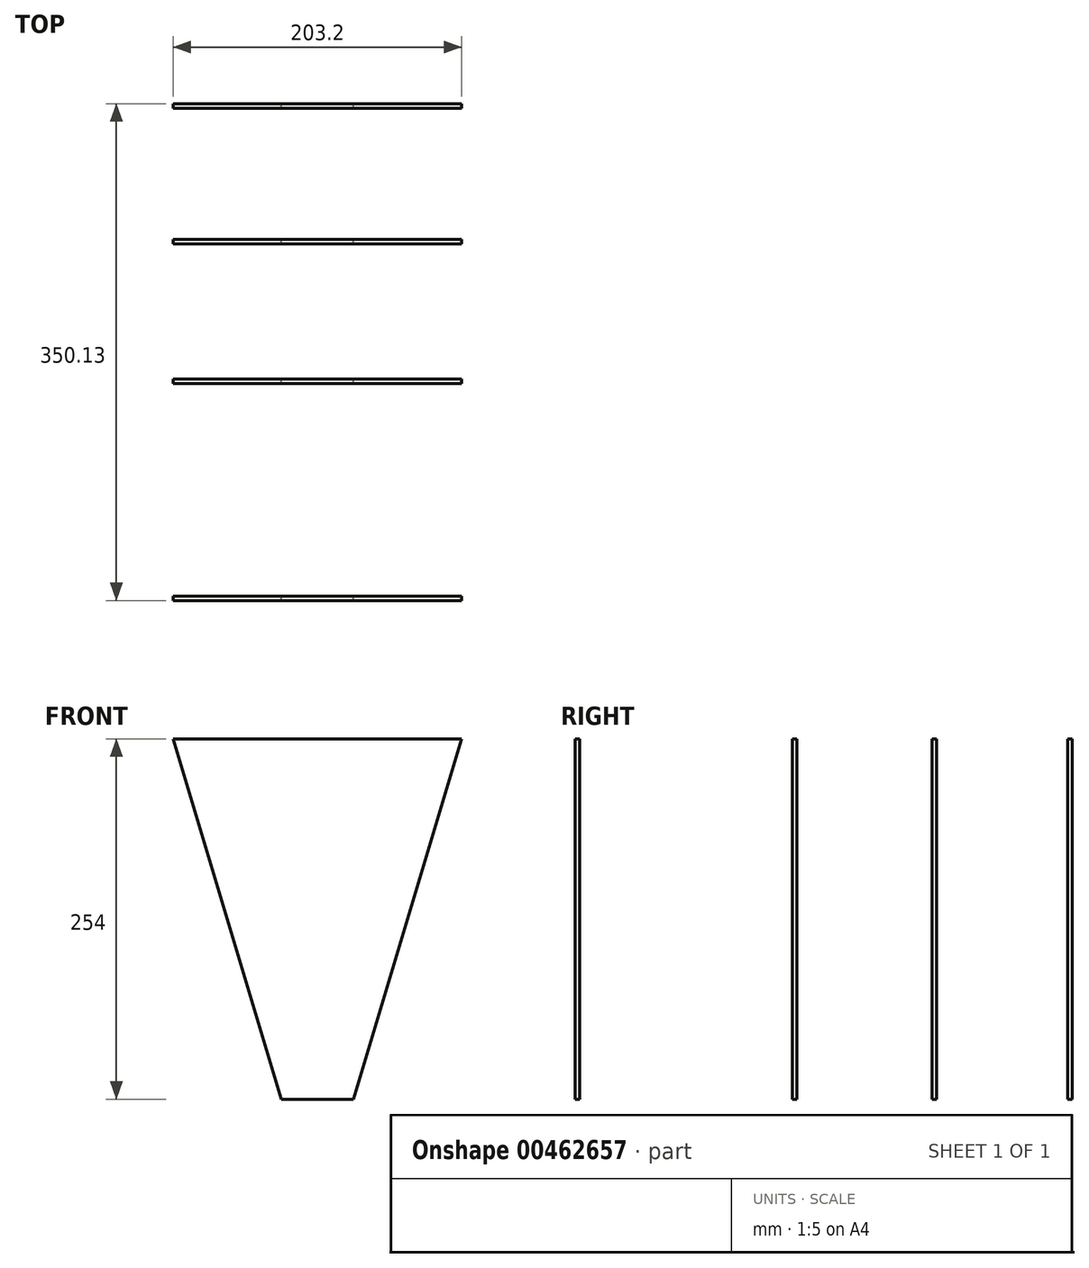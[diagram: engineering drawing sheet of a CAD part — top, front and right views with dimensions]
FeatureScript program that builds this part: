
annotation { "Feature Type Name" : "Feature", "Feature Type Description" : "" }
export const myFeature = defineFeature(function(context is Context, id is Id, definition is map)
    precondition{}
    {
        {
            var Q0;
            Q0=qCreatedBy(makeId("Front.planeOp"),FACE);
            var sketch = newSketch(context, id + "F0", { "sketchPlane" : qUnion([Q0])});
            skLineSegment(sketch, "E0", {"start": v(0, 37.13) * mm, "end": v(-101.6, 37.13) * mm});
            skLineSegment(sketch, "E1", {"start": v(0, 37.13) * mm, "end": v(101.6, 37.13) * mm});
            skLineSegment(sketch, "E2", {"start": v(-25.4, -216.87) * mm, "end": v(25.4, -216.87) * mm});
            skLineSegment(sketch, "E3", {"start": v(-101.6, 37.13) * mm, "end": v(-25.4, -216.87) * mm});
            skLineSegment(sketch, "E4", {"start": v(25.4, -216.87) * mm, "end": v(101.6, 37.13) * mm});
            skSolve(sketch);
        }
        {
            var Q0;
            Q0=makeQuery(id+"F0.imprint","IMPRINT",FACE,{"disambiguationData":[TD([[makeQuery(id+"F0.imprint","IMPRINT",EDGE,{"derivedFrom":sQuery(id+"F0.wireOp",EDGE,"E0")}),1.0]])]});
            extrude(context, id + "F1", {"entities" : qUnion([Q0]), "depth" : 3.17 * mm});
        }
        {
            var Q0;
            Q0=makeQuery(id+"F1.opExtrude","SWEPT_BODY",BODY,{"disambiguationData":[OSD([sQuery(id+"F0.wireOp",EDGE,"E0"),sQuery(id+"F0.wireOp",EDGE,"E1"),sQuery(id+"F0.wireOp",EDGE,"E2"),sQuery(id+"F0.wireOp",EDGE,"E3"),sQuery(id+"F0.wireOp",EDGE,"E4")])]});
            transform(context, id + "F2", {"entities" : qUnion([Q0]), "transformType" : TransformType.TRANSLATION_3D, "dx" : 0 * mm, "dy" : 152.9 * mm, "dz" : 0 * mm, "makeCopy" : true});
        }
        {
            var Q0;
            Q0=makeQuery(id+"F2.opPattern","COPY",BODY,{"derivedFrom":makeQuery(id+"F1.opExtrude","SWEPT_BODY",BODY,{"disambiguationData":[OSD([sQuery(id+"F0.wireOp",EDGE,"E0"),sQuery(id+"F0.wireOp",EDGE,"E1"),sQuery(id+"F0.wireOp",EDGE,"E2"),sQuery(id+"F0.wireOp",EDGE,"E3"),sQuery(id+"F0.wireOp",EDGE,"E4")])]}),"instanceName":"1"});
            transform(context, id + "F3", {"entities" : qUnion([Q0]), "transformType" : TransformType.TRANSLATION_3D, "dx" : 0 * mm, "dy" : 98.55 * mm, "dz" : 0 * mm, "makeCopy" : true});
        }
        {
            var Q0;
            Q0=makeQuery(id+"F3.opPattern","COPY",BODY,{"derivedFrom":makeQuery(id+"F2.opPattern","COPY",BODY,{"derivedFrom":makeQuery(id+"F1.opExtrude","SWEPT_BODY",BODY,{"disambiguationData":[OSD([sQuery(id+"F0.wireOp",EDGE,"E0"),sQuery(id+"F0.wireOp",EDGE,"E1"),sQuery(id+"F0.wireOp",EDGE,"E2"),sQuery(id+"F0.wireOp",EDGE,"E3"),sQuery(id+"F0.wireOp",EDGE,"E4")])]}),"instanceName":"1"}),"instanceName":"1"});
            transform(context, id + "F4", {"entities" : qUnion([Q0]), "transformType" : TransformType.TRANSLATION_3D, "dx" : 0 * mm, "dy" : 95.5 * mm, "dz" : 0 * mm, "makeCopy" : true});
        }
    });
